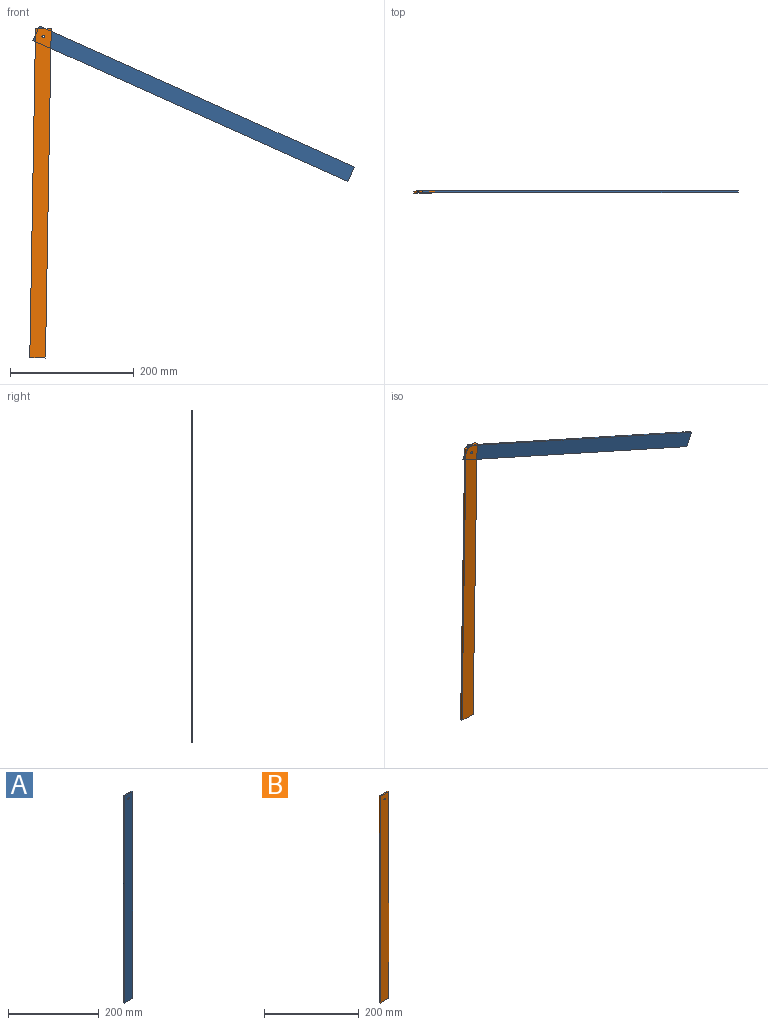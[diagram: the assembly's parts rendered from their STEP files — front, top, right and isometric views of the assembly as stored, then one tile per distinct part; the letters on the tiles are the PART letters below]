
ASSEMBLY  parts=2 mates=1
PART A: 7 faces, bbox 25.4x3.2x558.8 mm
  f0: plane 558.8x3.18mm, normal (-1,0,0), area 1774.2mm2, adj f1,f4,f5,f6
  f1: plane 25.4x3.18mm, normal (0,0,-1), area 80.6mm2, adj f0,f2,f5,f6
  f2: plane 558.8x3.18mm, normal (1,0,0), area 1774.2mm2, adj f1,f4,f5,f6
  f3: cylinder r=2.11mm len=4.22mm, axis (0,1,0), area 42.1mm2, adj f5,f6
  f4: plane 25.4x3.18mm, normal (0,0,1), area 80.6mm2, adj f0,f2,f5,f6
  f5: plane 558.8x25.4mm, normal (0,-1,0), area 14179.6mm2, adj f0,f1,f2,f3,f4
  f6: plane 558.8x25.4mm, normal (0,1,0), area 14179.6mm2, adj f0,f1,f2,f3,f4
PART B: 7 faces, bbox 25.4x3.2x533.4 mm
  f0: plane 25.4x3.18mm, normal (0,0,-1), area 80.6mm2, adj f1,f4,f5,f6
  f1: plane 533.4x3.18mm, normal (1,0,0), area 1693.5mm2, adj f0,f2,f5,f6
  f2: plane 25.4x3.18mm, normal (0,0,1), area 80.6mm2, adj f1,f4,f5,f6
  f3: cylinder r=2.11mm len=4.22mm, axis (0,1,0), area 42.1mm2, adj f5,f6
  f4: plane 533.4x3.18mm, normal (-1,0,0), area 1693.5mm2, adj f0,f2,f5,f6
  f5: plane 533.4x25.4mm, normal (0,-1,0), area 13534.4mm2, adj f0,f1,f2,f3,f4
  f6: plane 533.4x25.4mm, normal (0,1,0), area 13534.4mm2, adj f0,f1,f2,f3,f4
PLACE A rot(axis=(0,-1,0),65.9deg) t=(258.92,3.18,394.82)mm
PLACE B rot(axis=(0,1,0),1deg) t=(17.37,3.17,266.44)mm
MATE revolute B.f3 <-> A.f3  axis (0,-1,0) through (9.12,0,520.62)mm
